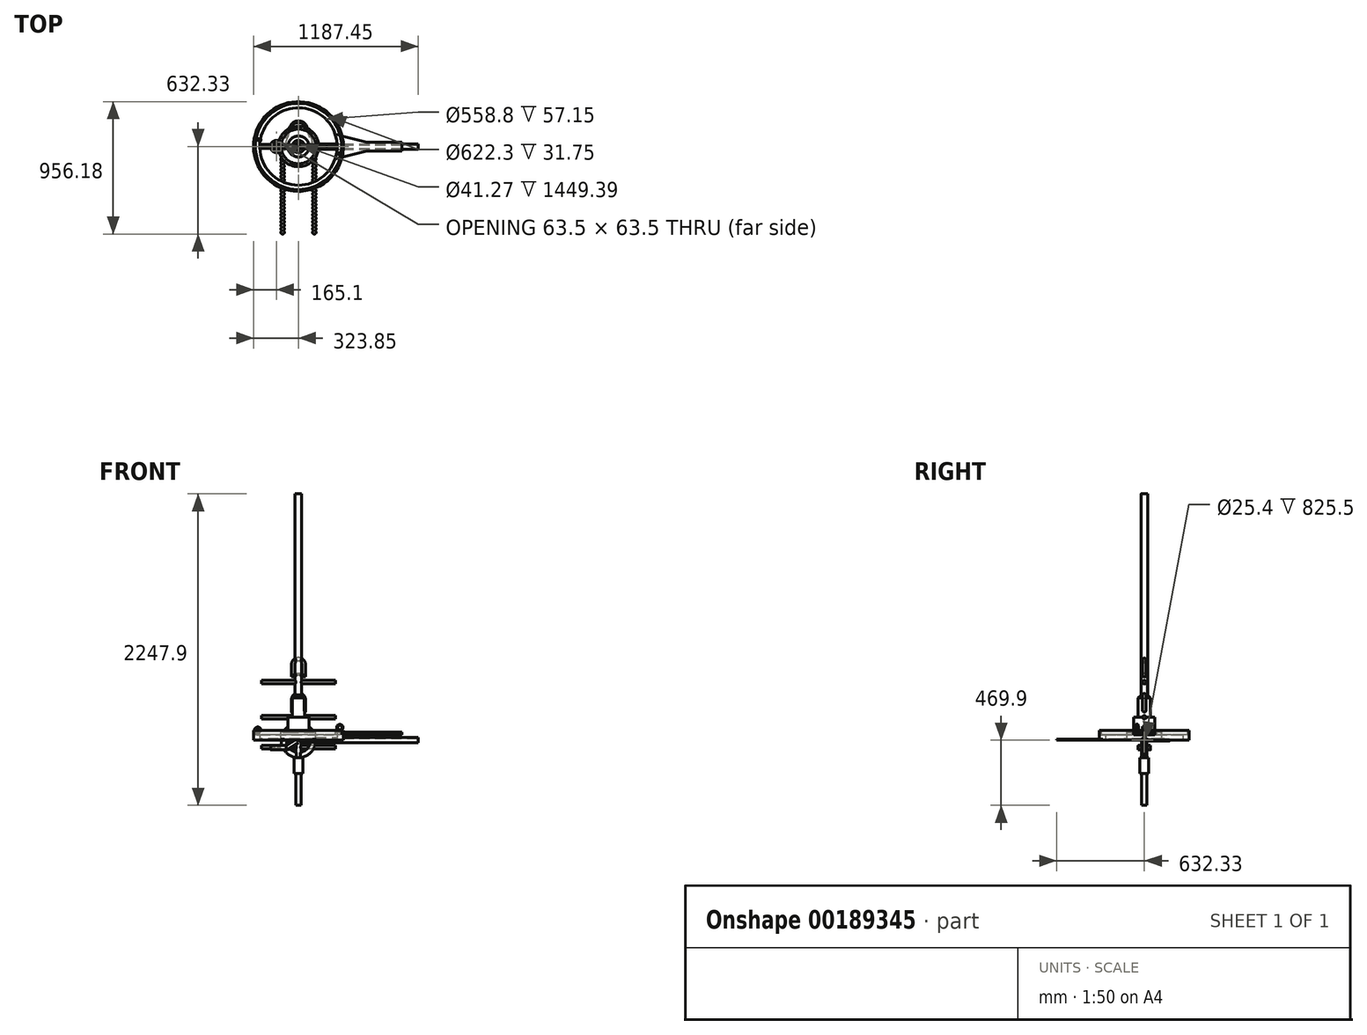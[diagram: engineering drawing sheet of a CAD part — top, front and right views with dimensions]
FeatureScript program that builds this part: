
annotation { "Feature Type Name" : "Feature", "Feature Type Description" : "" }
export const myFeature = defineFeature(function(context is Context, id is Id, definition is map)
    precondition{}
    {
        {
            var Q0;
            Q0=qCreatedBy(makeId("Top.planeOp"),FACE);
            var sketch = newSketch(context, id + "F0", { "sketchPlane" : qUnion([Q0])});
            skCircle(sketch, "E0", {"center": v(0, 0) * mm, "radius": 279.4 * mm});
            skCircle(sketch, "E1", {"center": v(0, 0) * mm, "radius": 317.5 * mm});
            skPoint(sketch, "E2", {"position": v(-139.7, -241.97) * mm});
            skLineSegment(sketch, "E3", {"start": v(0, 0) * mm, "end": v(-279.4, 0) * mm, "construction": true});
            skLineSegment(sketch, "E4", {"start": v(0, 0) * mm, "end": v(-139.7, -241.97) * mm, "construction": true});
            skSolve(sketch);
        }
        {
            var Q0;
            Q0 = qSketchRegion(id + "F0", true);
            extrude(context, id + "F1", {"entities" : qUnion([Q0]), "depth" : 38.1 * mm});
        }
        {
            var Q0;
            Q0=makeQuery(id+"F1.opExtrude","CAP_FACE",FACE,{"disambiguationData":[OSD([sQuery(id+"F0.wireOp",EDGE,"E0"),sQuery(id+"F0.wireOp",EDGE,"E1")])],"isStart":false});
            var sketch = newSketch(context, id + "F2", { "sketchPlane" : qUnion([Q0])});
            skArc(sketch, "E5.0", {"start": v(264.88, -88.9) * mm, "mid": v(279.4, 0) * mm, "end": v(264.88, 88.9) * mm});
            skLineSegment(sketch, "E6", {"start": v(0, 0) * mm, "end": v(747.48, 0) * mm, "construction": true});
            skLineSegment(sketch, "E7", {"start": v(747.48, 0) * mm, "end": v(747.48, 31.75) * mm});
            skLineSegment(sketch, "E8", {"start": v(747.48, 31.75) * mm, "end": v(493.48, 31.75) * mm});
            skLineSegment(sketch, "E9", {"start": v(493.48, 31.75) * mm, "end": v(264.88, 88.9) * mm});
            skLineSegment(sketch, "E10.MirrorCS", {"start": v(493.48, -31.75) * mm, "end": v(264.88, -88.9) * mm});
            skLineSegment(sketch, "E11.MirrorCS", {"start": v(747.48, 0) * mm, "end": v(747.48, -31.75) * mm});
            skLineSegment(sketch, "E12.MirrorCS", {"start": v(747.48, -31.75) * mm, "end": v(493.48, -31.75) * mm});
            skSolve(sketch);
        }
        {
            var Q0;
            Q0 = qSketchRegion(id + "F2", true);
            extrude(context, id + "F3", {"entities" : qUnion([Q0]), "operationType" : NewBodyOperationType.ADD, "depth" : 19.05 * mm});
        }
        {
            var Q0;
            Q0=qCreatedBy(makeId("Front.planeOp"),FACE);
            var sketch = newSketch(context, id + "F4", { "sketchPlane" : qUnion([Q0])});
            skCircle(sketch, "E13", {"center": v(302.98, 91.62) * mm, "radius": 16.33 * mm});
            skArc(sketch, "E14", {"start": v(309.33, 69.85) * mm, "mid": v(302.98, 114.3) * mm, "end": v(296.63, 69.85) * mm});
            skLineSegment(sketch, "E15.top", {"start": v(296.63, 57.15) * mm, "end": v(309.33, 57.15) * mm});
            skLineSegment(sketch, "E15.left", {"start": v(296.63, 69.85) * mm, "end": v(296.63, 57.15) * mm});
            skLineSegment(sketch, "E15.right", {"start": v(309.33, 69.85) * mm, "end": v(309.33, 57.15) * mm});
            skLineSegment(sketch, "E16", {"start": v(302.98, 114.3) * mm, "end": v(337.77, 114.3) * mm, "construction": true});
            skCircle(sketch, "E17", {"center": v(-298.45, 72.57) * mm, "radius": 16.33 * mm});
            skArc(sketch, "E18", {"start": v(-292.1, 50.8) * mm, "mid": v(-298.45, 95.25) * mm, "end": v(-304.8, 50.8) * mm});
            skLineSegment(sketch, "E19.top", {"start": v(-304.8, 38.1) * mm, "end": v(-292.1, 38.1) * mm});
            skLineSegment(sketch, "E19.left", {"start": v(-304.8, 50.8) * mm, "end": v(-304.8, 38.1) * mm});
            skLineSegment(sketch, "E19.right", {"start": v(-292.1, 50.8) * mm, "end": v(-292.1, 38.1) * mm});
            skLineSegment(sketch, "E20", {"start": v(-298.45, 95.25) * mm, "end": v(47.59, 95.25) * mm, "construction": true});
            skLineSegment(sketch, "E21", {"start": v(0, 0) * mm, "end": v(0, 240.36) * mm, "construction": true});
            skSolve(sketch);
        }
        {
            var Q0;
            Q0 = qSketchRegion(id + "F4", true);
            extrude(context, id + "F5", {"entities" : qUnion([Q0]), "depth" : 12.7 * mm, "symmetric" : true});
        }
        {
            var Q0;
            Q0=makeQuery(id+"F5.opExtrude","SWEPT_BODY",BODY,{"disambiguationData":[OSD([sQuery(id+"F4.wireOp",EDGE,"E13"),sQuery(id+"F4.wireOp",EDGE,"E14"),sQuery(id+"F4.wireOp",EDGE,"E15.top"),sQuery(id+"F4.wireOp",EDGE,"E15.left"),sQuery(id+"F4.wireOp",EDGE,"E15.right")])]});
            var Q1;
            Q1=makeQuery(id+"F5.opExtrude","SWEPT_BODY",BODY,{"disambiguationData":[OSD([sQuery(id+"F4.wireOp",EDGE,"E17"),sQuery(id+"F4.wireOp",EDGE,"E18"),sQuery(id+"F4.wireOp",EDGE,"E19.top"),sQuery(id+"F4.wireOp",EDGE,"E19.left"),sQuery(id+"F4.wireOp",EDGE,"E19.right")])]});
            var Q2;
            Q2=sQuery(id+"F4.wireOp",EDGE,"E21");
            transform(context, id + "F6", {"entities" : qUnion([Q0, Q1]), "transformType" : TransformType.ROTATION, "transformAxis" : qUnion([Q2]), "angle" : 10 * degree, "oppositeDirection" : true, "makeCopy" : false});
        }
        {
            var Q0;
            Q0=qCreatedBy(makeId("Top.planeOp"),FACE);
            var sketch = newSketch(context, id + "F7", { "sketchPlane" : qUnion([Q0])});
            skCircle(sketch, "E22", {"center": v(0, 0) * mm, "radius": 323.85 * mm});
            skCircle(sketch, "E23", {"center": v(0, 0) * mm, "radius": 311.15 * mm});
            skPoint(sketch, "E24", {"position": v(0, 311.15) * mm});
            skSolve(sketch);
        }
        {
            var Q0;
            Q0 = qSketchRegion(id + "F7", true);
            extrude(context, id + "F8", {"entities" : qUnion([Q0]), "depth" : 69.85 * mm});
        }
        {
            var Q0;
            Q0=qCreatedBy(makeId("Front.planeOp"),FACE);
            var sketch = newSketch(context, id + "F9", { "sketchPlane" : qUnion([Q0])});
            skLineSegment(sketch, "E25", {"start": v(0, 0) * mm, "end": v(863.6, 0) * mm});
            skLineSegment(sketch, "E26", {"start": v(0, 19.05) * mm, "end": v(0, -19.05) * mm});
            skLineSegment(sketch, "E27.bottom", {"start": v(-203.2, -38.1) * mm, "end": v(-88.9, -38.1) * mm});
            skLineSegment(sketch, "E27.top", {"start": v(-203.2, -69.85) * mm, "end": v(-79.02, -69.85) * mm});
            skLineSegment(sketch, "E27.left", {"start": v(-203.2, -38.1) * mm, "end": v(-203.2, -69.85) * mm});
            skLineSegment(sketch, "E28", {"start": v(0, 19.05) * mm, "end": v(-88.9, -38.1) * mm});
            skLineSegment(sketch, "E29", {"start": v(0, -19.05) * mm, "end": v(-79.02, -69.85) * mm});
            skSolve(sketch);
        }
        {
            var Q0;
            Q0=makeQuery(id+"F9.imprint","IMPRINT",FACE,{"disambiguationData":[TD([[makeQuery(id+"F9.imprint","IMPRINT",EDGE,{"derivedFrom":sQuery(id+"F9.wireOp",EDGE,"E27.bottom")}),-1.0]])]});
            extrude(context, id + "F10", {"entities" : qUnion([Q0]), "depth" : 88.9 * mm, "symmetric" : true});
        }
        {
            var Q0;
            Q0=makeQuery(id+"F10.opExtrude","SWEPT_FACE",FACE,{"disambiguationData":[OSD([sQuery(id+"F9.wireOp",EDGE,"E26")])]});
            var sketch = newSketch(context, id + "F11", { "sketchPlane" : qUnion([Q0])});
            skCircle(sketch, "E30", {"center": v(0, 0) * mm, "radius": 12.7 * mm});
            skCircle(sketch, "E31", {"center": v(0, 0) * mm, "radius": 19.05 * mm});
            skSolve(sketch);
        }
        {
            var Q0;
            Q0 = qSketchRegion(id + "F11", true);
            var Q1;
            Q1=sQuery(id+"F9.wireOp",EDGE,"E25");
            sweep(context, id + "F12", {"operationType" : NewBodyOperationType.ADD, "profiles" : qUnion([Q0]), "path" : qUnion([Q1])});
        }
        {
            var Q0;
            Q0=qCreatedBy(makeId("Top.planeOp"),FACE);
            var sketch = newSketch(context, id + "F13", { "sketchPlane" : qUnion([Q0])});
            skArc(sketch, "E32", {"start": v(-141.65, 41.03) * mm, "mid": v(-183.4, 36.98) * mm, "end": v(-203.2, 0) * mm});
            skLineSegment(sketch, "E33.bottom", {"start": v(0.02, 19.05) * mm, "end": v(-88.9, 19.05) * mm});
            skLineSegment(sketch, "E34", {"start": v(-141.65, 41.03) * mm, "end": v(-88.9, 19.05) * mm});
            skLineSegment(sketch, "E35", {"start": v(0, 0) * mm, "end": v(-158.75, 0) * mm, "construction": true});
            skCircle(sketch, "E36.cCircle", {"center": v(-158.75, 0) * mm, "radius": 31.75 * mm, "construction": true});
            skLineSegment(sketch, "E36.0", {"start": v(-167.26, 31.75) * mm, "end": v(-150.24, 31.75) * mm});
            skLineSegment(sketch, "E36.1", {"start": v(-150.24, 31.75) * mm, "end": v(-135.5, 23.24) * mm});
            skLineSegment(sketch, "E36.2", {"start": v(-135.5, 23.24) * mm, "end": v(-127, 8.5) * mm});
            skLineSegment(sketch, "E36.3", {"start": v(-127, 8.5) * mm, "end": v(-127, -8.5) * mm});
            skLineSegment(sketch, "E36.4", {"start": v(-127, -8.5) * mm, "end": v(-135.5, -23.24) * mm});
            skLineSegment(sketch, "E36.5", {"start": v(-135.5, -23.24) * mm, "end": v(-150.24, -31.75) * mm});
            skLineSegment(sketch, "E36.6", {"start": v(-150.24, -31.75) * mm, "end": v(-167.26, -31.75) * mm});
            skLineSegment(sketch, "E36.7", {"start": v(-167.26, -31.75) * mm, "end": v(-182, -23.24) * mm});
            skLineSegment(sketch, "E36.8", {"start": v(-182, -23.24) * mm, "end": v(-190.5, -8.5) * mm});
            skLineSegment(sketch, "E36.9", {"start": v(-190.5, -8.5) * mm, "end": v(-190.5, 8.5) * mm});
            skLineSegment(sketch, "E36.10", {"start": v(-190.5, 8.5) * mm, "end": v(-182, 23.24) * mm});
            skLineSegment(sketch, "E36.11", {"start": v(-182, 23.24) * mm, "end": v(-167.26, 31.75) * mm});
            skPoint(sketch, "E36.0.midPoint", {"position": v(-158.75, 31.75) * mm});
            skLineSegment(sketch, "E37", {"start": v(0.02, 19.05) * mm, "end": v(0.02, 44.45) * mm});
            skLineSegment(sketch, "E38", {"start": v(0.02, 44.45) * mm, "end": v(-158.75, 44.45) * mm});
            skLineSegment(sketch, "E39", {"start": v(-158.75, 44.45) * mm, "end": v(-203.2, 44.45) * mm});
            skLineSegment(sketch, "E40", {"start": v(-203.2, 44.45) * mm, "end": v(-203.2, 0) * mm});
            skLineSegment(sketch, "E41", {"start": v(863.6, -19.05) * mm, "end": v(0, -19.05) * mm, "construction": true});
            skLineSegment(sketch, "E42", {"start": v(0, 19.05) * mm, "end": v(863.6, 19.05) * mm, "construction": true});
            skLineSegment(sketch, "E43.MirrorCS", {"start": v(0.02, -19.05) * mm, "end": v(0.02, -44.45) * mm});
            skLineSegment(sketch, "E44.MirrorCS", {"start": v(0.02, -19.05) * mm, "end": v(-88.9, -19.05) * mm});
            skLineSegment(sketch, "E45.MirrorCS", {"start": v(0.02, -44.45) * mm, "end": v(-158.75, -44.45) * mm});
            skLineSegment(sketch, "E46.MirrorCS", {"start": v(-141.65, -41.03) * mm, "end": v(-88.9, -19.05) * mm});
            skArc(sketch, "E47.MirrorCS", {"start": v(-141.65, -41.03) * mm, "mid": v(-183.4, -36.98) * mm, "end": v(-203.2, 0) * mm});
            skLineSegment(sketch, "E48.MirrorCS", {"start": v(-203.2, -44.45) * mm, "end": v(-203.2, 0) * mm});
            skLineSegment(sketch, "E49.MirrorCS", {"start": v(-158.75, -44.45) * mm, "end": v(-203.2, -44.45) * mm});
            skSolve(sketch);
        }
        {
            var Q0;
            Q0 = qSketchRegion(id + "F13", true);
            extrude(context, id + "F14", {"entities" : qUnion([Q0]), "operationType" : NewBodyOperationType.REMOVE, "endBound" : BoundingType.THROUGH_ALL, "oppositeDirection" : true, "depth" : 25.4 * mm, "hasSecondDirection" : true, "secondDirectionBound" : BoundingType.THROUGH_ALL, "secondDirectionOppositeDirection" : false, "secondDirectionDepth" : 25.4 * mm});
        }
        {
            var Q0;
            Q0=qCreatedBy(makeId("Front.planeOp"),FACE);
            var sketch = newSketch(context, id + "F15", { "sketchPlane" : qUnion([Q0])});
            skLineSegment(sketch, "E50.bottom", {"start": v(0, 0) * mm, "end": v(76.2, 0) * mm});
            skLineSegment(sketch, "E50.top", {"start": v(44.45, 165.1) * mm, "end": v(76.2, 165.1) * mm});
            skLineSegment(sketch, "E50.right", {"start": v(76.2, 0) * mm, "end": v(76.2, 165.1) * mm});
            skLineSegment(sketch, "E51.right", {"start": v(44.45, 165.1) * mm, "end": v(44.45, 304.8) * mm});
            skLineSegment(sketch, "E52.top", {"start": v(0, 469.9) * mm, "end": v(19.05, 469.9) * mm});
            skLineSegment(sketch, "E52.right", {"start": v(19.05, 330.2) * mm, "end": v(19.05, 469.9) * mm});
            skLineSegment(sketch, "E53", {"start": v(19.05, 330.2) * mm, "end": v(44.45, 304.8) * mm});
            skLineSegment(sketch, "E54", {"start": v(0, 469.9) * mm, "end": v(0, 0) * mm});
            skLineSegment(sketch, "E55", {"start": v(0, 0) * mm, "end": v(0, -149.17) * mm, "construction": true});
            skSolve(sketch);
        }
        {
            var Q0;
            Q0 = qSketchRegion(id + "F15", true);
            var Q1;
            Q1=sQuery(id+"F15.wireOp",EDGE,"E55");
            revolve(context, id + "F16", {"entities" : qUnion([Q0]), "axis" : qUnion([Q1]), "revolveType" : RevolveType.FULL});
        }
        {
            var Q0;
            Q0=qCreatedBy(makeId("Right.planeOp"),FACE);
            var sketch = newSketch(context, id + "F17", { "sketchPlane" : qUnion([Q0])});
            skCircle(sketch, "E56", {"center": v(0, 419.1) * mm, "radius": 12.7 * mm});
            skLineSegment(sketch, "E57", {"start": v(19.05, 584.2) * mm, "end": v(19.05, 330.2) * mm, "construction": true});
            skLineSegment(sketch, "E58", {"start": v(-19.05, 330.2) * mm, "end": v(-19.05, 584.2) * mm, "construction": true});
            skSolve(sketch);
        }
        {
            var Q0;
            Q0=qCreatedBy(makeId("Front.planeOp"),FACE);
            var sketch = newSketch(context, id + "F18", { "sketchPlane" : qUnion([Q0])});
            skLineSegment(sketch, "E59", {"start": v(0, 508) * mm, "end": v(0, 546.1) * mm, "construction": true});
            skArc(sketch, "E60.0.endCap", {"start": v(-38.1, 546.1) * mm, "mid": v(0, 584.2) * mm, "end": v(38.1, 546.1) * mm});
            skLineSegment(sketch, "E61", {"start": v(0, 584.2) * mm, "end": v(73.3, 584.2) * mm, "construction": true});
            skPoint(sketch, "E62", {"position": v(0, 469.9) * mm});
            skLineSegment(sketch, "E63", {"start": v(0, 508) * mm, "end": v(0, 469.9) * mm, "construction": true});
            skLineSegment(sketch, "E64", {"start": v(-38.1, 546.1) * mm, "end": v(-38.1, 469.9) * mm});
            skLineSegment(sketch, "E65", {"start": v(-38.1, 469.9) * mm, "end": v(0, 469.9) * mm});
            skLineSegment(sketch, "E66", {"start": v(38.1, 546.1) * mm, "end": v(38.1, 469.9) * mm});
            skLineSegment(sketch, "E67", {"start": v(38.1, 469.9) * mm, "end": v(0, 469.9) * mm});
            skSolve(sketch);
        }
        {
            var Q0;
            Q0=qCreatedBy(makeId("Right.planeOp"),FACE);
            var sketch = newSketch(context, id + "F19", { "sketchPlane" : qUnion([Q0])});
            skCircle(sketch, "E68", {"center": v(0, 469.9) * mm, "radius": 12.7 * mm});
            skSolve(sketch);
        }
        {
            var Q0;
            Q0 = qSketchRegion(id + "F19", true);
            var Q1;
            Q1 = qConstructionFilter(qBodyType(qCreatedBy(id + "F18" ,EDGE), BodyType.WIRE), ConstructionObject.NO);
            sweep(context, id + "F20", {"operationType" : NewBodyOperationType.ADD, "profiles" : qUnion([Q0]), "path" : qUnion([Q1])});
        }
        {
            var Q0;
            Q0 = qSketchRegion(id + "F17", true);
            extrude(context, id + "F21", {"entities" : qUnion([Q0]), "operationType" : NewBodyOperationType.ADD, "depth" : 533.4 * mm, "symmetric" : true});
        }
        {
            var Q0;
            Q0=qCreatedBy(makeId("Front.planeOp"),FACE);
            var sketch = newSketch(context, id + "F22", { "sketchPlane" : qUnion([Q0])});
            skLineSegment(sketch, "E69", {"start": v(0, 0) * mm, "end": v(0, 215.9) * mm});
            skLineSegment(sketch, "E70", {"start": v(0, 215.9) * mm, "end": v(19.05, 215.9) * mm});
            skLineSegment(sketch, "E71", {"start": v(19.05, 215.9) * mm, "end": v(19.05, 107.95) * mm});
            skLineSegment(sketch, "E72", {"start": v(19.05, 107.95) * mm, "end": v(31.75, 107.95) * mm});
            skLineSegment(sketch, "E73", {"start": v(31.75, 107.95) * mm, "end": v(31.75, 57.15) * mm});
            skLineSegment(sketch, "E74", {"start": v(31.75, 57.15) * mm, "end": v(125.41, 57.15) * mm});
            skLineSegment(sketch, "E75", {"start": v(125.41, 57.15) * mm, "end": v(125.41, 0) * mm});
            skLineSegment(sketch, "E76", {"start": v(125.41, 0) * mm, "end": v(0, 0) * mm});
            skLineSegment(sketch, "E77", {"start": v(0, 0) * mm, "end": v(0, -70.4) * mm, "construction": true});
            skSolve(sketch);
        }
        {
            var Q0;
            Q0 = qSketchRegion(id + "F22", true);
            var Q1;
            Q1=sQuery(id+"F22.wireOp",EDGE,"E77");
            revolve(context, id + "F23", {"entities" : qUnion([Q0]), "axis" : qUnion([Q1]), "revolveType" : RevolveType.FULL});
        }
        {
            var Q0;
            Q0=qCreatedBy(makeId("Front.planeOp"),FACE);
            var sketch = newSketch(context, id + "F24", { "sketchPlane" : qUnion([Q0])});
            skLineSegment(sketch, "E78", {"start": v(0, 260.62) * mm, "end": v(0, 292.1) * mm, "construction": true});
            skArc(sketch, "E79.0.endCap", {"start": v(-38.1, 292.1) * mm, "mid": v(0, 330.2) * mm, "end": v(38.1, 292.1) * mm});
            skLineSegment(sketch, "E80", {"start": v(0, 330.2) * mm, "end": v(73.3, 330.2) * mm, "construction": true});
            skPoint(sketch, "E81", {"position": v(0, 215.9) * mm});
            skLineSegment(sketch, "E82", {"start": v(0, 260.62) * mm, "end": v(0, 215.9) * mm, "construction": true});
            skLineSegment(sketch, "E83", {"start": v(-38.1, 292.1) * mm, "end": v(-38.1, 215.9) * mm});
            skLineSegment(sketch, "E84", {"start": v(-38.1, 215.9) * mm, "end": v(0, 215.9) * mm});
            skLineSegment(sketch, "E85", {"start": v(38.1, 292.1) * mm, "end": v(38.1, 215.9) * mm});
            skLineSegment(sketch, "E86", {"start": v(38.1, 215.9) * mm, "end": v(0, 215.9) * mm});
            skLineSegment(sketch, "E87", {"start": v(0, 215.9) * mm, "end": v(0, 0) * mm, "construction": true});
            skSolve(sketch);
        }
        {
            var Q0;
            Q0=qCreatedBy(makeId("Right.planeOp"),FACE);
            var sketch = newSketch(context, id + "F25", { "sketchPlane" : qUnion([Q0])});
            skCircle(sketch, "E88", {"center": v(0, 215.9) * mm, "radius": 12.7 * mm});
            skCircle(sketch, "E89", {"center": v(0, 165.1) * mm, "radius": 12.7 * mm});
            skSolve(sketch);
        }
        {
            var Q0;
            Q0=makeQuery(id+"F25.imprint","IMPRINT",FACE,{"disambiguationData":[TD([[makeQuery(id+"F25.imprint","IMPRINT",EDGE,{"derivedFrom":sQuery(id+"F25.wireOp",EDGE,"E88")}),1.0]])]});
            var Q1;
            Q1 = qConstructionFilter(qBodyType(qCreatedBy(id + "F24" ,EDGE), BodyType.WIRE), ConstructionObject.NO);
            sweep(context, id + "F26", {"operationType" : NewBodyOperationType.ADD, "profiles" : qUnion([Q0]), "path" : qUnion([Q1])});
        }
        {
            var Q0;
            Q0=makeQuery(id+"F25.imprint","IMPRINT",FACE,{"disambiguationData":[TD([[makeQuery(id+"F25.imprint","IMPRINT",EDGE,{"derivedFrom":sQuery(id+"F25.wireOp",EDGE,"E89")}),1.0]])]});
            var Q1;
            Q1=sQuery(id+"F25.wireOp",EDGE,"E89");
            extrude(context, id + "F27", {"entities" : qUnion([Q0]), "operationType" : NewBodyOperationType.ADD, "surfaceEntities" : qUnion([Q1]), "depth" : 533.4 * mm, "symmetric" : true});
        }
        {
            var Q0;
            Q0=qCreatedBy(makeId("Top.planeOp"),FACE);
            var sketch = newSketch(context, id + "F28", { "sketchPlane" : qUnion([Q0])});
            skCircle(sketch, "E90", {"center": v(0, 0) * mm, "radius": 23.81 * mm});
            skCircle(sketch, "E91", {"center": v(0, 0) * mm, "radius": 20.64 * mm});
            skSolve(sketch);
        }
        {
            var Q0;
            Q0 = qSketchRegion(id + "F28", true);
            extrude(context, id + "F29", {"entities" : qUnion([Q0]), "depth" : 1778 * mm});
        }
        {
            var Q0;
            Q0=qCreatedBy(makeId("Top.planeOp"),FACE);
            var sketch = newSketch(context, id + "F30", { "sketchPlane" : qUnion([Q0])});
            skArc(sketch, "E92", {"start": v(-145.35, -14.29) * mm, "mid": v(0, -146.05) * mm, "end": v(145.35, -14.29) * mm});
            skCircle(sketch, "E93", {"center": v(0, 0) * mm, "radius": 117.48 * mm});
            skLineSegment(sketch, "E94.bottom", {"start": v(311.15, 14.29) * mm, "end": v(145.35, 14.29) * mm});
            skLineSegment(sketch, "E94.top", {"start": v(311.15, -14.29) * mm, "end": v(145.35, -14.29) * mm});
            skLineSegment(sketch, "E94.left", {"start": v(311.15, 14.29) * mm, "end": v(311.15, -14.29) * mm});
            skLineSegment(sketch, "E94.right", {"start": v(-311.15, 14.29) * mm, "end": v(-311.15, -14.29) * mm});
            skLineSegment(sketch, "E95.trimOffspring", {"start": v(-145.35, 14.29) * mm, "end": v(-311.15, 14.29) * mm});
            skLineSegment(sketch, "E96.trimOffspring", {"start": v(-145.35, -14.29) * mm, "end": v(-311.15, -14.29) * mm});
            skArc(sketch, "E97.trimOffspring", {"start": v(145.35, 14.29) * mm, "mid": v(0, 146.05) * mm, "end": v(-145.35, 14.29) * mm});
            skLineSegment(sketch, "E98", {"start": v(0, 117.48) * mm, "end": v(0, 146.05) * mm, "construction": true});
            skPoint(sketch, "E99", {"position": v(-117.48, 0) * mm});
            skSolve(sketch);
        }
        {
            var Q0;
            Q0 = qSketchRegion(id + "F30", true);
            extrude(context, id + "F31", {"entities" : qUnion([Q0]), "depth" : 9.52 * mm});
        }
        {
            var Q0;
            Q0=qCreatedBy(makeId("Top.planeOp"),FACE);
            var sketch = newSketch(context, id + "F32", { "sketchPlane" : qUnion([Q0])});
            skCircle(sketch, "E100", {"center": v(0, 0) * mm, "radius": 28.58 * mm});
            skLineSegment(sketch, "E101", {"start": v(0, 0) * mm, "end": v(0, 28.58) * mm, "construction": true});
            skLineSegment(sketch, "E102", {"start": v(-30.48, 37.47) * mm, "end": v(-121.92, -31.12) * mm});
            skLineSegment(sketch, "E103", {"start": v(-114.3, -53.98) * mm, "end": v(0, -53.98) * mm});
            skPoint(sketch, "E104.visualSharp", {"position": v(-152.4, -53.98) * mm});
            skArc(sketch, "E104.filletArc", {"start": v(-121.92, -31.12) * mm, "mid": v(-126.35, -45.3) * mm, "end": v(-114.3, -53.98) * mm});
            skCircle(sketch, "E105", {"center": v(-114.3, -66.42) * mm, "radius": 12.7 * mm});
            skCircle(sketch, "E106.1.0.0", {"center": v(-114.3, -91.57) * mm, "radius": 12.7 * mm});
            skCircle(sketch, "E106.2.0.0", {"center": v(-114.3, -116.71) * mm, "radius": 12.7 * mm});
            skLineSegment(sketch, "E106.direction1", {"start": v(-114.3, -66.42) * mm, "end": v(-114.3, -91.57) * mm, "construction": true});
            skCircle(sketch, "E107.0.3.0", {"center": v(-114.3, -141.86) * mm, "radius": 12.7 * mm});
            skCircle(sketch, "E107.0.4.0", {"center": v(-114.3, -167) * mm, "radius": 12.7 * mm});
            skCircle(sketch, "E107.0.5.0", {"center": v(-114.3, -192.15) * mm, "radius": 12.7 * mm});
            skCircle(sketch, "E107.0.6.0", {"center": v(-114.3, -217.3) * mm, "radius": 12.7 * mm});
            skCircle(sketch, "E107.0.7.0", {"center": v(-114.3, -242.44) * mm, "radius": 12.7 * mm});
            skCircle(sketch, "E107.0.8.0", {"center": v(-114.3, -267.59) * mm, "radius": 12.7 * mm});
            skCircle(sketch, "E107.0.9.0", {"center": v(-114.3, -292.73) * mm, "radius": 12.7 * mm});
            skCircle(sketch, "E107.0.10.0", {"center": v(-114.3, -317.88) * mm, "radius": 12.7 * mm});
            skCircle(sketch, "E107.0.11.0", {"center": v(-114.3, -343.03) * mm, "radius": 12.7 * mm});
            skCircle(sketch, "E107.0.12.0", {"center": v(-114.3, -368.17) * mm, "radius": 12.7 * mm});
            skCircle(sketch, "E107.0.13.0", {"center": v(-114.3, -393.32) * mm, "radius": 12.7 * mm});
            skCircle(sketch, "E107.0.14.0", {"center": v(-114.3, -418.46) * mm, "radius": 12.7 * mm});
            skCircle(sketch, "E107.0.15.0", {"center": v(-114.3, -443.61) * mm, "radius": 12.7 * mm});
            skCircle(sketch, "E107.0.16.0", {"center": v(-114.3, -468.76) * mm, "radius": 12.7 * mm});
            skCircle(sketch, "E107.0.17.0", {"center": v(-114.3, -493.9) * mm, "radius": 12.7 * mm});
            skCircle(sketch, "E107.0.18.0", {"center": v(-114.3, -519.05) * mm, "radius": 12.7 * mm});
            skCircle(sketch, "E107.0.19.0", {"center": v(-114.3, -544.2) * mm, "radius": 12.7 * mm});
            skCircle(sketch, "E107.0.20.0", {"center": v(-114.3, -569.34) * mm, "radius": 12.7 * mm});
            skCircle(sketch, "E107.0.21.0", {"center": v(-114.3, -594.49) * mm, "radius": 12.7 * mm});
            skCircle(sketch, "E107.0.22.0", {"center": v(-114.3, -619.63) * mm, "radius": 12.7 * mm});
            skArc(sketch, "E108.MirrorCS", {"start": v(121.92, -31.12) * mm, "mid": v(126.35, -45.3) * mm, "end": v(114.3, -53.98) * mm});
            skCircle(sketch, "E109.MirrorC", {"center": v(114.3, -66.42) * mm, "radius": 12.7 * mm});
            skCircle(sketch, "E110.MirrorC", {"center": v(114.3, -91.57) * mm, "radius": 12.7 * mm});
            skCircle(sketch, "E111.MirrorC", {"center": v(114.3, -569.34) * mm, "radius": 12.7 * mm});
            skCircle(sketch, "E112.MirrorC", {"center": v(114.3, -317.88) * mm, "radius": 12.7 * mm});
            skCircle(sketch, "E113.MirrorC", {"center": v(114.3, -167) * mm, "radius": 12.7 * mm});
            skCircle(sketch, "E114.MirrorC", {"center": v(114.3, -141.86) * mm, "radius": 12.7 * mm});
            skCircle(sketch, "E115.MirrorC", {"center": v(114.3, -418.46) * mm, "radius": 12.7 * mm});
            skCircle(sketch, "E116.MirrorC", {"center": v(114.3, -519.05) * mm, "radius": 12.7 * mm});
            skCircle(sketch, "E117.MirrorC", {"center": v(114.3, -368.17) * mm, "radius": 12.7 * mm});
            skCircle(sketch, "E118.MirrorC", {"center": v(114.3, -292.73) * mm, "radius": 12.7 * mm});
            skCircle(sketch, "E119.MirrorC", {"center": v(114.3, -468.76) * mm, "radius": 12.7 * mm});
            skCircle(sketch, "E120.MirrorC", {"center": v(114.3, -267.59) * mm, "radius": 12.7 * mm});
            skCircle(sketch, "E121.MirrorC", {"center": v(114.3, -493.9) * mm, "radius": 12.7 * mm});
            skCircle(sketch, "E122.MirrorC", {"center": v(114.3, -594.49) * mm, "radius": 12.7 * mm});
            skCircle(sketch, "E123.MirrorC", {"center": v(114.3, -343.03) * mm, "radius": 12.7 * mm});
            skCircle(sketch, "E124.MirrorC", {"center": v(114.3, -619.63) * mm, "radius": 12.7 * mm});
            skCircle(sketch, "E125.MirrorC", {"center": v(114.3, -443.61) * mm, "radius": 12.7 * mm});
            skCircle(sketch, "E126.MirrorC", {"center": v(114.3, -116.71) * mm, "radius": 12.7 * mm});
            skCircle(sketch, "E127.MirrorC", {"center": v(114.3, -393.32) * mm, "radius": 12.7 * mm});
            skCircle(sketch, "E128.MirrorC", {"center": v(114.3, -192.15) * mm, "radius": 12.7 * mm});
            skCircle(sketch, "E129.MirrorC", {"center": v(114.3, -217.3) * mm, "radius": 12.7 * mm});
            skCircle(sketch, "E130.MirrorC", {"center": v(114.3, -544.2) * mm, "radius": 12.7 * mm});
            skCircle(sketch, "E131.MirrorC", {"center": v(114.3, -242.44) * mm, "radius": 12.7 * mm});
            skLineSegment(sketch, "E132.MirrorCS", {"start": v(30.48, 37.47) * mm, "end": v(121.92, -31.12) * mm});
            skLineSegment(sketch, "E133.MirrorCS", {"start": v(114.3, -53.98) * mm, "end": v(0, -53.98) * mm});
            skPoint(sketch, "E134.MirrorP", {"position": v(152.4, -53.98) * mm});
            skPoint(sketch, "E135.visualSharp", {"position": v(0, 60.33) * mm});
            skArc(sketch, "E135.filletArc", {"start": v(30.48, 37.46) * mm, "mid": v(0, 47.62) * mm, "end": v(-30.48, 37.46) * mm});
            skPoint(sketch, "E136", {"position": v(0, 28.58) * mm});
            skSolve(sketch);
        }
        {
            var Q0;
            Q0 = qSketchRegion(id + "F32", true);
            extrude(context, id + "F33", {"entities" : qUnion([Q0]), "depth" : 6.35 * mm});
        }
        {
            var Q0;
            Q0=qCreatedBy(makeId("Front.planeOp"),FACE);
            var sketch = newSketch(context, id + "F34", { "sketchPlane" : qUnion([Q0])});
            skCircle(sketch, "E137", {"center": v(0, -0.95) * mm, "radius": 87.31 * mm});
            skCircle(sketch, "E138", {"center": v(0, -0.95) * mm, "radius": 125.41 * mm});
            skSolve(sketch);
        }
        {
            var Q0;
            Q0 = qSketchRegion(id + "F34", true);
            extrude(context, id + "F35", {"entities" : qUnion([Q0]), "depth" : 12.7 * mm});
        }
        {
            var Q0;
            Q0=qCreatedBy(makeId("Top.planeOp"),FACE);
            var sketch = newSketch(context, id + "F36", { "sketchPlane" : qUnion([Q0])});
            skLineSegment(sketch, "E139", {"start": v(0, 0) * mm, "end": v(0, 177.8) * mm, "construction": true});
            skFitSpline(sketch, "E140", {"points": [v(0, 177.8) * mm, v(-40.64, 163.32) * mm, v(-106.36, 0) * mm], "startDerivative": vector(-139.85, 0) * mm, "endDerivative": vector(-111.45, -331.81) * mm});
            skLineSegment(sketch, "E141", {"start": v(0, 177.8) * mm, "end": v(-62.22, 177.8) * mm, "construction": true});
            skPoint(sketch, "E142.trimOffspring.end.orphan", {"position": v(125.41, 0) * mm});
            skPoint(sketch, "E143.0.0.start.orphan", {"position": v(-125.41, 0) * mm});
            skLineSegment(sketch, "E144", {"start": v(-125.41, 0) * mm, "end": v(-87.31, 0) * mm, "construction": true});
            skFitSpline(sketch, "E145.MirrorCS", {"points": [v(0, 177.8) * mm, v(40.64, 163.32) * mm, v(106.36, 0) * mm], "startDerivative": vector(139.85, 0) * mm, "endDerivative": vector(111.45, -331.81) * mm});
            skSolve(sketch);
        }
        {
            var Q0;
            Q0=makeQuery(id+"F35.opExtrude","CAP_FACE",FACE,{"disambiguationData":[OSD([sQuery(id+"F34.wireOp",EDGE,"E137"),sQuery(id+"F34.wireOp",EDGE,"E138")])],"isStart":true});
            var sketch = newSketch(context, id + "F37", { "sketchPlane" : qUnion([Q0])});
            skCircle(sketch, "E146", {"center": v(106.36, 0) * mm, "radius": 6.35 * mm});
            skSolve(sketch);
        }
        {
            var Q0;
            Q0 = qSketchRegion(id + "F37", true);
            var Q1;
            Q1 = qConstructionFilter(qBodyType(qCreatedBy(id + "F36" ,EDGE), BodyType.WIRE), ConstructionObject.NO);
            sweep(context, id + "F38", {"operationType" : NewBodyOperationType.ADD, "profiles" : qUnion([Q0]), "path" : qUnion([Q1])});
        }
        {
            var Q0;
            Q0=qCreatedBy(makeId("Front.planeOp"),FACE);
            var sketch = newSketch(context, id + "F39", { "sketchPlane" : qUnion([Q0])});
            skLineSegment(sketch, "E147.bottom", {"start": v(0, 0) * mm, "end": v(19.05, 0) * mm});
            skLineSegment(sketch, "E147.top", {"start": v(0, -469.9) * mm, "end": v(19.05, -469.9) * mm});
            skLineSegment(sketch, "E147.left", {"start": v(0, 0) * mm, "end": v(0, -469.9) * mm});
            skLineSegment(sketch, "E147.right", {"start": v(19.05, 0) * mm, "end": v(19.05, -127) * mm});
            skLineSegment(sketch, "E148.bottom", {"start": v(19.05, -127) * mm, "end": v(31.75, -127) * mm});
            skLineSegment(sketch, "E148.top", {"start": v(19.05, -241.3) * mm, "end": v(31.75, -241.3) * mm});
            skLineSegment(sketch, "E148.right", {"start": v(31.75, -127) * mm, "end": v(31.75, -241.3) * mm});
            skLineSegment(sketch, "E149.trimOffspring", {"start": v(19.05, -241.3) * mm, "end": v(19.05, -469.9) * mm});
            skLineSegment(sketch, "E150", {"start": v(0, 0) * mm, "end": v(0, 51.17) * mm, "construction": true});
            skSolve(sketch);
        }
        {
            var Q0;
            Q0 = qSketchRegion(id + "F39", true);
            var Q1;
            Q1=sQuery(id+"F39.wireOp",EDGE,"E150");
            revolve(context, id + "F40", {"entities" : qUnion([Q0]), "axis" : qUnion([Q1]), "revolveType" : RevolveType.FULL});
        }
        {
            var Q0;
            Q0=qCreatedBy(makeId("Front.planeOp"),FACE);
            var sketch = newSketch(context, id + "F41", { "sketchPlane" : qUnion([Q0])});
            skLineSegment(sketch, "E151", {"start": v(0, 76.2) * mm, "end": v(0, 185.62) * mm, "construction": true});
            skArc(sketch, "E152.0.endCap", {"start": v(-38.1, 76.2) * mm, "mid": v(0, 114.3) * mm, "end": v(38.1, 76.2) * mm});
            skLineSegment(sketch, "E153", {"start": v(0, 114.3) * mm, "end": v(233.54, 114.3) * mm, "construction": true});
            skPoint(sketch, "E154", {"position": v(0, 0) * mm});
            skLineSegment(sketch, "E155", {"start": v(0, 185.62) * mm, "end": v(0, 0) * mm, "construction": true});
            skLineSegment(sketch, "E156", {"start": v(-38.1, 76.2) * mm, "end": v(-38.1, 0) * mm});
            skLineSegment(sketch, "E157", {"start": v(-38.1, 0) * mm, "end": v(0, 0) * mm});
            skLineSegment(sketch, "E158", {"start": v(38.1, 76.2) * mm, "end": v(38.1, 0) * mm});
            skLineSegment(sketch, "E159", {"start": v(38.1, 0) * mm, "end": v(0, 0) * mm});
            skSolve(sketch);
        }
        {
            var Q0;
            Q0=qCreatedBy(makeId("Right.planeOp"),FACE);
            var sketch = newSketch(context, id + "F42", { "sketchPlane" : qUnion([Q0])});
            skCircle(sketch, "E160", {"center": v(0, 0) * mm, "radius": 12.7 * mm});
            skCircle(sketch, "E161", {"center": v(0, -50.8) * mm, "radius": 12.7 * mm});
            skSolve(sketch);
        }
        {
            var Q0;
            Q0=makeQuery(id+"F42.imprint","IMPRINT",FACE,{"disambiguationData":[TD([[makeQuery(id+"F42.imprint","IMPRINT",EDGE,{"derivedFrom":sQuery(id+"F42.wireOp",EDGE,"E160")}),1.0]])]});
            var Q1;
            Q1=sQuery(id+"F42.wireOp",EDGE,"E160");
            var Q2;
            Q2 = qConstructionFilter(qBodyType(qCreatedBy(id + "F41" ,EDGE), BodyType.WIRE), ConstructionObject.NO);
            sweep(context, id + "F43", {"operationType" : NewBodyOperationType.ADD, "profiles" : qUnion([Q0]), "surfaceProfiles" : qUnion([Q1]), "path" : qUnion([Q2])});
        }
        {
            var Q0;
            Q0=makeQuery(id+"F42.imprint","IMPRINT",FACE,{"disambiguationData":[TD([[makeQuery(id+"F42.imprint","IMPRINT",EDGE,{"derivedFrom":sQuery(id+"F42.wireOp",EDGE,"E161")}),1.0]])]});
            var Q1;
            Q1=sQuery(id+"F42.wireOp",EDGE,"E161");
            extrude(context, id + "F44", {"entities" : qUnion([Q0]), "operationType" : NewBodyOperationType.ADD, "surfaceEntities" : qUnion([Q1]), "depth" : 533.4 * mm, "symmetric" : true});
        }
    });
